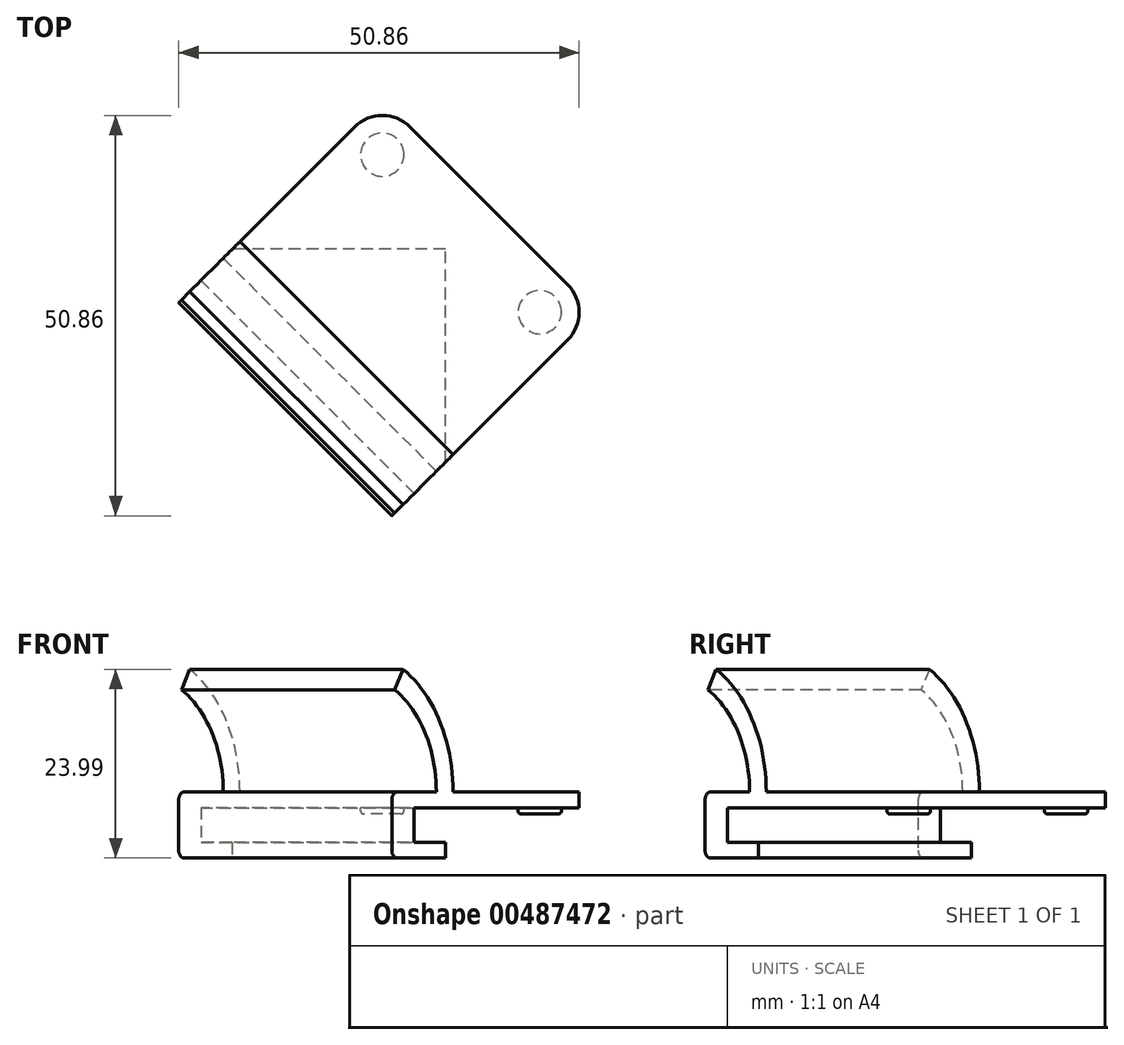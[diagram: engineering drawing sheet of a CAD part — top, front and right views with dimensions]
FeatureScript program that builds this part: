
annotation { "Feature Type Name" : "Feature", "Feature Type Description" : "" }
export const myFeature = defineFeature(function(context is Context, id is Id, definition is map)
    precondition{}
    {
        {
            var Q0;
            Q0=qCreatedBy(makeId("Top.planeOp"),FACE);
            var sketch = newSketch(context, id + "F0", { "sketchPlane" : qUnion([Q0])});
            skLineSegment(sketch, "E0", {"start": v(20, 20) * mm, "end": v(-39, 20) * mm});
            skLineSegment(sketch, "E1", {"start": v(-39, 20) * mm, "end": v(-39, 0) * mm});
            skLineSegment(sketch, "E2", {"start": v(-39, 0) * mm, "end": v(0, -39) * mm});
            skLineSegment(sketch, "E3", {"start": v(0, -39) * mm, "end": v(20, -39) * mm});
            skLineSegment(sketch, "E4", {"start": v(20, -39) * mm, "end": v(20, 20) * mm});
            skCircle(sketch, "E5", {"center": v(-10, 10) * mm, "radius": 2.75 * mm});
            skCircle(sketch, "E6", {"center": v(10, -10) * mm, "radius": 2.75 * mm});
            skLineSegment(sketch, "E7", {"start": v(0, 0) * mm, "end": v(-34.24, -34.24) * mm, "construction": true});
            skSolve(sketch);
        }
        {
            var Q0;
            Q0=qCreatedBy(makeId("Top.planeOp"),FACE);
            var sketch = newSketch(context, id + "F1", { "sketchPlane" : qUnion([Q0])});
            skLineSegment(sketch, "E8", {"start": v(17.07, -10) * mm, "end": v(-10, 17.07) * mm});
            skLineSegment(sketch, "E9", {"start": v(-10, 17.07) * mm, "end": v(-35.86, -8.8) * mm});
            skLineSegment(sketch, "E10", {"start": v(-35.86, -8.8) * mm, "end": v(-8.8, -35.86) * mm});
            skLineSegment(sketch, "E11", {"start": v(-8.8, -35.86) * mm, "end": v(17.07, -10) * mm});
            skSolve(sketch);
        }
        {
            var Q0;
            Q0=makeQuery(id+"F1.imprint","IMPRINT",FACE,{"disambiguationData":[TD([[makeQuery(id+"F1.imprint","IMPRINT",EDGE,{"derivedFrom":sQuery(id+"F1.wireOp",EDGE,"E8")}),1.0]])]});
            extrude(context, id + "F2", {"entities" : qUnion([Q0]), "depth" : 2 * mm, "hasSecondDirection" : true, "secondDirectionOppositeDirection" : true, "secondDirectionDepth" : 6.4 * mm});
        }
        {
            var Q0;
            Q0=makeQuery(id+"F2.opExtrude","SWEPT_FACE",FACE,{"disambiguationData":[OSD([sQuery(id+"F1.wireOp",EDGE,"E11")])]});
            var sketch = newSketch(context, id + "F3", { "sketchPlane" : qUnion([Q0])});
            skLineSegment(sketch, "E12.bottom", {"start": v(5, 0) * mm, "end": v(-27.58, 0) * mm});
            skLineSegment(sketch, "E12.top", {"start": v(5, -4.4) * mm, "end": v(-27.58, -4.4) * mm});
            skLineSegment(sketch, "E12.left", {"start": v(5, 0) * mm, "end": v(5, -4.4) * mm});
            skLineSegment(sketch, "E12.right", {"start": v(-27.58, 0) * mm, "end": v(-27.58, -4.4) * mm});
            skSolve(sketch);
        }
        {
            var Q0;
            Q0=makeQuery(id+"F3.imprint","IMPRINT",FACE,{"disambiguationData":[TD([[makeQuery(id+"F3.imprint","IMPRINT",EDGE,{"derivedFrom":sQuery(id+"F3.wireOp",EDGE,"E12.bottom")}),1.0]])]});
            extrude(context, id + "F4", {"entities" : qUnion([Q0]), "operationType" : NewBodyOperationType.REMOVE, "endBound" : BoundingType.THROUGH_ALL, "oppositeDirection" : true, "depth" : 25 * mm});
        }
        {
            var Q0;
            Q0=sQuery(id+"F0.wireOp",EDGE,"E7");
            cPlane(context, id + "F5", {"entities" : qUnion([Q0]), "cplaneType" : CPlaneType.LINE_ANGLE, "offset" : 25 * mm, "angle" : 90 * degree, "width" : 150 * mm, "height" : 150 * mm});
        }
        {
            var Q0;
            Q0=qCreatedBy(id+"F5.planeOp",FACE);
            var sketch = newSketch(context, id + "F6", { "sketchPlane" : qUnion([Q0])});
            skLineSegment(sketch, "E13.0", {"start": v(-31.58, 2) * mm, "end": v(5, 2) * mm, "construction": true});
            skLineSegment(sketch, "E14.0", {"start": v(-31.58, 2) * mm, "end": v(-31.58, -6.4) * mm, "construction": true});
            skArc(sketch, "E15", {"start": v(-20.58, 2) * mm, "mid": v(-22.99, 11) * mm, "end": v(-29.58, 17.59) * mm});
            skArc(sketch, "E16", {"start": v(-23.58, 2) * mm, "mid": v(-25.59, 9.5) * mm, "end": v(-31.08, 15) * mm});
            skLineSegment(sketch, "E17", {"start": v(-31.08, 15) * mm, "end": v(-29.58, 17.59) * mm});
            skLineSegment(sketch, "E18", {"start": v(-20.58, 2) * mm, "end": v(-23.58, 2) * mm});
            skSolve(sketch);
        }
        {
            var Q0;
            Q0 = qSketchRegion(id + "F6", true);
            var Q1;
            Q1=makeQuery(id+"F2.opExtrude","SWEPT_FACE",FACE,{"disambiguationData":[OSD([sQuery(id+"F1.wireOp",EDGE,"E9")])]});
            var Q2;
            Q2=makeQuery(id+"F2.opExtrude","SWEPT_FACE",FACE,{"disambiguationData":[OSD([sQuery(id+"F1.wireOp",EDGE,"E11")])]});
            extrude(context, id + "F7", {"entities" : qUnion([Q0]), "operationType" : NewBodyOperationType.ADD, "endBound" : BoundingType.UP_TO_SURFACE, "oppositeDirection" : true, "endBoundEntityFace" : qUnion([Q1]), "depth" : 38.5 * mm, "hasSecondDirection" : true, "secondDirectionBound" : SecondDirectionBoundingType.UP_TO_SURFACE, "secondDirectionOppositeDirection" : false, "secondDirectionBoundEntityFace" : qUnion([Q2]), "secondDirectionDepth" : 25 * mm});
        }
        {
            var Q0;
            Q0=makeQuery(id+"F2.opExtrude","CAP_FACE",FACE,{"disambiguationData":[OSD([sQuery(id+"F1.wireOp",EDGE,"E8"),sQuery(id+"F1.wireOp",EDGE,"E9"),sQuery(id+"F1.wireOp",EDGE,"E10"),sQuery(id+"F1.wireOp",EDGE,"E11")])],"isStart":true});
            var sketch = newSketch(context, id + "F8", { "sketchPlane" : qUnion([Q0])});
            skLineSegment(sketch, "E19", {"start": v(-2, 29.07) * mm, "end": v(-2, 2) * mm});
            skLineSegment(sketch, "E20", {"start": v(-2, 2) * mm, "end": v(-29.07, 2) * mm});
            skLineSegment(sketch, "E21.0", {"start": v(-10, -17.07) * mm, "end": v(-35.86, 8.8) * mm});
            skLineSegment(sketch, "E22.0", {"start": v(17.07, 10) * mm, "end": v(-10, -17.07) * mm});
            skLineSegment(sketch, "E23.0", {"start": v(-8.8, 35.86) * mm, "end": v(17.07, 10) * mm});
            skSolve(sketch);
        }
        {
            var Q0;
            {var subQ3=sQuery(id+"F8.wireOp",EDGE,"E19");Q0=makeQuery(id+"F8.imprint","IMPRINT",FACE,{"disambiguationData":[TD([[makeQuery(id+"F8.imprint","IMPRINT",EDGE,{"derivedFrom":subQ3}),1.0]])]});}
            extrude(context, id + "F9", {"entities" : qUnion([Q0]), "operationType" : NewBodyOperationType.REMOVE, "endBound" : BoundingType.UP_TO_NEXT, "oppositeDirection" : true, "depth" : 25 * mm});
        }
        {
            var Q0;
            Q0=makeQuery(id+"F0.imprint","IMPRINT",FACE,{"disambiguationData":[TD([[makeQuery(id+"F0.imprint","IMPRINT",EDGE,{"derivedFrom":sQuery(id+"F0.wireOp",EDGE,"E6")}),1.0]])]});
            var Q1;
            Q1=makeQuery(id+"F0.imprint","IMPRINT",FACE,{"disambiguationData":[TD([[makeQuery(id+"F0.imprint","IMPRINT",EDGE,{"derivedFrom":sQuery(id+"F0.wireOp",EDGE,"E5")}),1.0]])]});
            extrude(context, id + "F10", {"entities" : qUnion([Q0, Q1]), "operationType" : NewBodyOperationType.ADD, "oppositeDirection" : true, "depth" : 0.8 * mm});
        }
        {
            var Q0;
            Q0=makeQuery(id+"F10.opExtrude","CAP_FACE",FACE,{"disambiguationData":[OSD([sQuery(id+"F0.wireOp",EDGE,"E6")])],"isStart":false});
            var Q1;
            Q1=makeQuery(id+"F10.opExtrude","CAP_FACE",FACE,{"disambiguationData":[OSD([sQuery(id+"F0.wireOp",EDGE,"E5")])],"isStart":false});
            fillet(context, id + "F11", {"entities" : qUnion([Q0, Q1]), "radius" : 0.4 * mm, "tangentPropagation" : true, "allowEdgeOverflow" : false});
        }
        {
            var Q0;
            Q0=makeQuery(id+"F7.opExtrude","TWEAK_EDGE",EDGE,{"derivedFrom":[makeQuery(id+"F6.imprint","IMPRINT",EDGE,{"derivedFrom":sQuery(id+"F6.wireOp",EDGE,"E16")}),makeQuery(id+"F6.imprint","IMPRINT",EDGE,{"derivedFrom":sQuery(id+"F6.wireOp",EDGE,"E17")})]});
            var Q1;
            Q1=makeQuery(id+"F7.opExtrude","TWEAK_EDGE",EDGE,{"derivedFrom":[makeQuery(id+"F6.imprint","IMPRINT",EDGE,{"derivedFrom":sQuery(id+"F6.wireOp",EDGE,"E15")}),makeQuery(id+"F6.imprint","IMPRINT",EDGE,{"derivedFrom":sQuery(id+"F6.wireOp",EDGE,"E17")})]});
            var Q2;
            Q2=makeQuery(id+"F2.opExtrude","CAP_EDGE",EDGE,{"disambiguationData":[OSD([sQuery(id+"F1.wireOp",EDGE,"E10")])],"isStart":false});
            var Q3;
            Q3=makeQuery(id+"F2.opExtrude","CAP_EDGE",EDGE,{"disambiguationData":[OSD([sQuery(id+"F1.wireOp",EDGE,"E10")])],"isStart":true});
            fillet(context, id + "F12", {"entities" : qUnion([Q0, Q1, Q2, Q3]), "radius" : 1 * mm, "tangentPropagation" : true, "allowEdgeOverflow" : false});
        }
        {
            var Q0;
            {var subQ0=sQuery(id+"F1.wireOp",EDGE,"E8");var subQ1=sQuery(id+"F1.wireOp",EDGE,"E11");Q0=makeQuery(id+"F4.boolean.opBoolean","SPLIT",EDGE,{"disambiguationData":[TD([makeQuery(id+"F4.opExtrude","SWEPT_FACE",FACE,{"disambiguationData":[OSD([sQuery(id+"F3.wireOp",EDGE,"E12.bottom")])]})])],"derivedFrom":makeQuery(id+"F2.opExtrude","SWEPT_EDGE",EDGE,{"disambiguationData":[OSD([subQ0,subQ1])]})});}
            var Q1;
            {var subQ0=sQuery(id+"F1.wireOp",EDGE,"E8");var subQ1=sQuery(id+"F1.wireOp",EDGE,"E9");Q1=makeQuery(id+"F4.boolean.opBoolean","SPLIT",EDGE,{"disambiguationData":[TD([makeQuery(id+"F4.opExtrude","SWEPT_FACE",FACE,{"disambiguationData":[OSD([sQuery(id+"F3.wireOp",EDGE,"E12.bottom")])]})])],"derivedFrom":makeQuery(id+"F2.opExtrude","SWEPT_EDGE",EDGE,{"disambiguationData":[OSD([subQ0,subQ1])]})});}
            fillet(context, id + "F13", {"entities" : qUnion([Q0, Q1]), "radius" : 5 * mm, "tangentPropagation" : true, "allowEdgeOverflow" : false});
        }
    });
